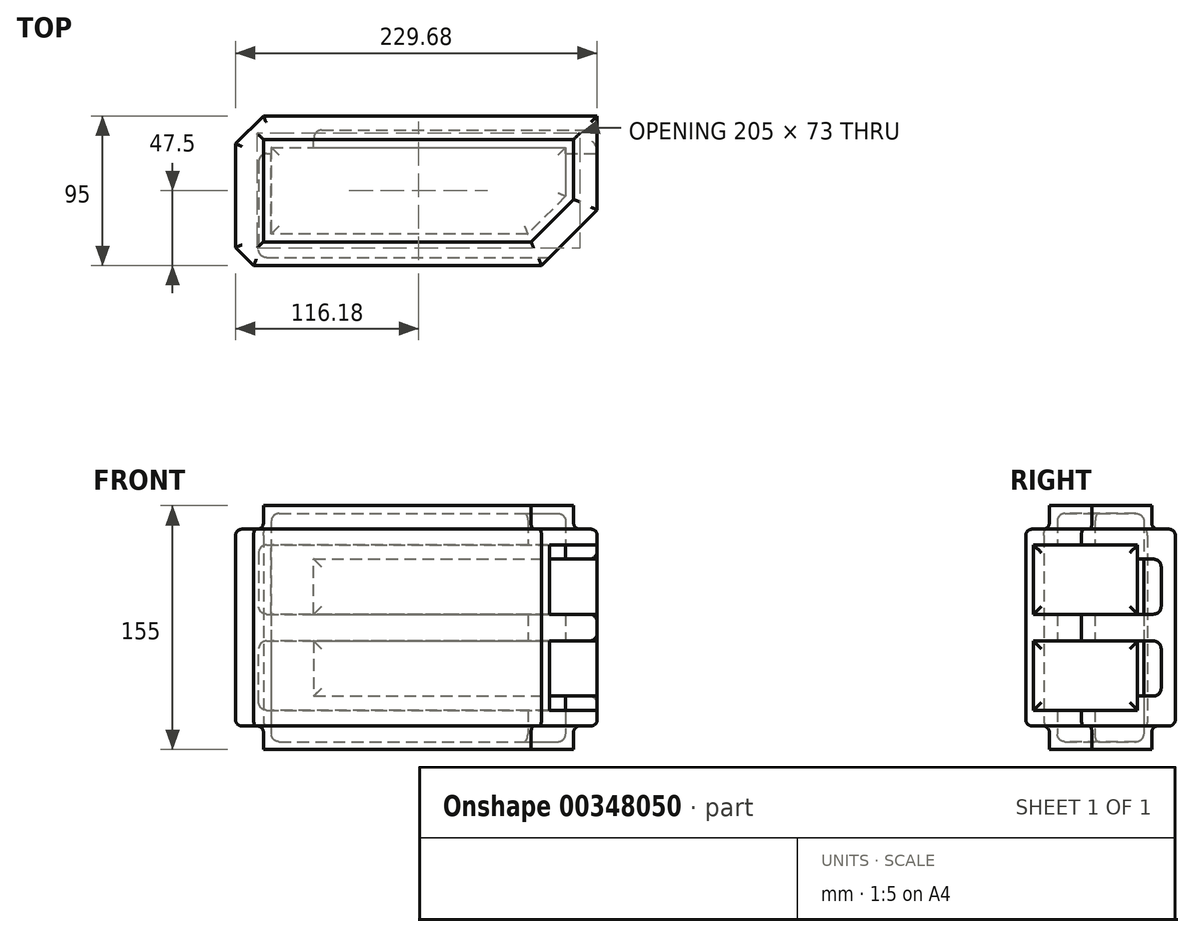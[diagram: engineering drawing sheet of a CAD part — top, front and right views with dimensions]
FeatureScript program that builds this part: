
annotation { "Feature Type Name" : "Feature", "Feature Type Description" : "" }
export const myFeature = defineFeature(function(context is Context, id is Id, definition is map)
    precondition{}
    {
        {
            var Q0;
            Q0=qCreatedBy(makeId("Top.planeOp"),FACE);
            var sketch = newSketch(context, id + "F0", { "sketchPlane" : qUnion([Q0])});
            skLineSegment(sketch, "E0", {"start": v(-103.21, -40) * mm, "end": v(79.64, -40) * mm});
            skPoint(sketch, "E1", {"position": v(0, -50) * mm});
            skLineSegment(sketch, "E2", {"start": v(79.64, -40) * mm, "end": v(115, -4.64) * mm});
            skLineSegment(sketch, "E3", {"start": v(115, -4.64) * mm, "end": v(115, 55) * mm});
            skLineSegment(sketch, "E4.2", {"start": v(100, 2) * mm, "end": v(100, 40) * mm});
            skLineSegment(sketch, "E4.4", {"start": v(73, -25) * mm, "end": v(100, 2) * mm});
            skLineSegment(sketch, "E4.5", {"start": v(-97, -25) * mm, "end": v(73, -25) * mm});
            skLineSegment(sketch, "E5.bottom", {"start": v(-97, 40) * mm, "end": v(100, 40) * mm});
            skLineSegment(sketch, "E5.left", {"start": v(-97, 40) * mm, "end": v(-97, -25) * mm});
            skLineSegment(sketch, "E6", {"start": v(-114.68, -28.54) * mm, "end": v(-114.68, 37.32) * mm});
            skLineSegment(sketch, "E7", {"start": v(-114.68, 37.32) * mm, "end": v(-97, 55) * mm});
            skLineSegment(sketch, "E8", {"start": v(-97, 55) * mm, "end": v(115, 55) * mm});
            skLineSegment(sketch, "E9", {"start": v(-114.68, -28.54) * mm, "end": v(-103.21, -40) * mm});
            skLineSegment(sketch, "E10.0", {"start": v(95, 4.07) * mm, "end": v(95, 35) * mm});
            skLineSegment(sketch, "E10.1", {"start": v(-92, 35) * mm, "end": v(95, 35) * mm});
            skLineSegment(sketch, "E10.2", {"start": v(70.93, -20) * mm, "end": v(95, 4.07) * mm});
            skLineSegment(sketch, "E10.3", {"start": v(-92, -20) * mm, "end": v(70.93, -20) * mm});
            skLineSegment(sketch, "E10.4", {"start": v(-92, 35) * mm, "end": v(-92, -20) * mm});
            skSolve(sketch);
        }
        {
            var Q0;
            Q0=makeQuery(id+"F0.imprint","IMPRINT",FACE,{"disambiguationData":[TD([[makeQuery(id+"F0.imprint","IMPRINT",EDGE,{"derivedFrom":sQuery(id+"F0.wireOp",EDGE,"E4.2")}),1.0]])]});
            var Q1;
            Q1=makeQuery(id+"F0.imprint","IMPRINT",FACE,{"disambiguationData":[TD([[makeQuery(id+"F0.imprint","IMPRINT",EDGE,{"derivedFrom":sQuery(id+"F0.wireOp",EDGE,"E10.0")}),1.0]])]});
            extrude(context, id + "F1", {"entities" : qUnion([Q0, Q1]), "depth" : (125 + 30) * mm, "offsetDistance" : 25 * mm});
        }
        {
            var Q0;
            Q0=makeQuery(id+"F0.imprint","IMPRINT",FACE,{"disambiguationData":[TD([[makeQuery(id+"F0.imprint","IMPRINT",EDGE,{"derivedFrom":sQuery(id+"F0.wireOp",EDGE,"E0")}),1.0]])]});
            extrude(context, id + "F2", {"entities" : qUnion([Q0]), "operationType" : NewBodyOperationType.ADD, "depth" : (155 - 15) * mm, "offsetDistance" : 25 * mm, "hasSecondDirection" : true, "secondDirectionOppositeDirection" : false, "secondDirectionDepth" : 15 * mm});
        }
        {
            var Q0;
            Q0=makeQuery(id+"F2.opExtrude","CAP_FACE",FACE,{"disambiguationData":[OSD([sQuery(id+"F0.wireOp",EDGE,"E0"),sQuery(id+"F0.wireOp",EDGE,"E2"),sQuery(id+"F0.wireOp",EDGE,"E3"),sQuery(id+"F0.wireOp",EDGE,"E4.2"),sQuery(id+"F0.wireOp",EDGE,"E4.4"),sQuery(id+"F0.wireOp",EDGE,"E5.bottom"),sQuery(id+"F0.wireOp",EDGE,"E4.5"),sQuery(id+"F0.wireOp",EDGE,"E5.left"),sQuery(id+"F0.wireOp",EDGE,"E6"),sQuery(id+"F0.wireOp",EDGE,"E7"),sQuery(id+"F0.wireOp",EDGE,"E8"),sQuery(id+"F0.wireOp",EDGE,"E9")])],"isStart":false});
            var Q1;
            Q1=makeQuery(id+"F2.opExtrude","CAP_FACE",FACE,{"disambiguationData":[OSD([sQuery(id+"F0.wireOp",EDGE,"E0"),sQuery(id+"F0.wireOp",EDGE,"E2"),sQuery(id+"F0.wireOp",EDGE,"E3"),sQuery(id+"F0.wireOp",EDGE,"E4.2"),sQuery(id+"F0.wireOp",EDGE,"E4.4"),sQuery(id+"F0.wireOp",EDGE,"E5.bottom"),sQuery(id+"F0.wireOp",EDGE,"E4.5"),sQuery(id+"F0.wireOp",EDGE,"E5.left"),sQuery(id+"F0.wireOp",EDGE,"E6"),sQuery(id+"F0.wireOp",EDGE,"E7"),sQuery(id+"F0.wireOp",EDGE,"E8"),sQuery(id+"F0.wireOp",EDGE,"E9")])],"isStart":true});
            fillet(context, id + "F3", {"entities" : qUnion([Q0, Q1]), "radius" : 4 * mm, "tangentPropagation" : true, "allowEdgeOverflow" : false});
        }
        {
            var Q0;
            Q0=makeQuery(id+"F2.opExtrude","SWEPT_FACE",FACE,{"disambiguationData":[OSD([sQuery(id+"F0.wireOp",EDGE,"E3")])]});
            var sketch = newSketch(context, id + "F4", { "sketchPlane" : qUnion([Q0])});
            skLineSegment(sketch, "E11.bottom", {"start": v(31, 130) * mm, "end": v(-35, 130) * mm});
            skLineSegment(sketch, "E11.top", {"start": v(31, 86) * mm, "end": v(-35, 86) * mm});
            skLineSegment(sketch, "E11.left", {"start": v(31, 130) * mm, "end": v(31, 86) * mm});
            skLineSegment(sketch, "E11.right", {"start": v(-35, 130) * mm, "end": v(-35, 86) * mm});
            skLineSegment(sketch, "E12.bottom", {"start": v(31, 25) * mm, "end": v(-35, 25) * mm});
            skLineSegment(sketch, "E12.top", {"start": v(31, 69) * mm, "end": v(-35, 69) * mm});
            skLineSegment(sketch, "E12.left", {"start": v(31, 25) * mm, "end": v(31, 69) * mm});
            skLineSegment(sketch, "E12.right", {"start": v(-35, 25) * mm, "end": v(-35, 69) * mm});
            skLineSegment(sketch, "E13.bottom", {"start": v(31, 86) * mm, "end": v(46, 86) * mm});
            skLineSegment(sketch, "E13.top", {"start": v(31, 121) * mm, "end": v(46, 121) * mm});
            skLineSegment(sketch, "E13.left", {"start": v(31, 86) * mm, "end": v(31, 121) * mm});
            skLineSegment(sketch, "E13.right", {"start": v(46, 86) * mm, "end": v(46, 121) * mm});
            skLineSegment(sketch, "E14.bottom", {"start": v(31, 69) * mm, "end": v(46, 69) * mm});
            skLineSegment(sketch, "E14.top", {"start": v(31, 34) * mm, "end": v(46, 34) * mm});
            skLineSegment(sketch, "E14.left", {"start": v(31, 69) * mm, "end": v(31, 34) * mm});
            skLineSegment(sketch, "E14.right", {"start": v(46, 69) * mm, "end": v(46, 34) * mm});
            skSolve(sketch);
        }
        {
            var Q0;
            {var subQ0=sQuery(id+"F4.wireOp",EDGE,"E11.left");Q0=makeQuery(id+"F4.imprint","IMPRINT",FACE,{"disambiguationData":[TD([[makeQuery(id+"F4.imprint","IMPRINT",EDGE,{"derivedFrom":subQ0}),-1.0]])]});}
            var Q1;
            {var subQ0=sQuery(id+"F4.wireOp",EDGE,"E11.right");Q1=makeQuery(id+"F4.imprint","IMPRINT",FACE,{"disambiguationData":[TD([[makeQuery(id+"F4.imprint","IMPRINT",EDGE,{"derivedFrom":subQ0}),1.0]])]});}
            var Q2;
            {var subQ0=sQuery(id+"F4.wireOp",EDGE,"E12.right");Q2=makeQuery(id+"F4.imprint","IMPRINT",FACE,{"disambiguationData":[TD([[makeQuery(id+"F4.imprint","IMPRINT",EDGE,{"derivedFrom":subQ0}),-1.0]])]});}
            var Q3;
            {var subQ0=sQuery(id+"F4.wireOp",EDGE,"E12.left");Q3=makeQuery(id+"F4.imprint","IMPRINT",FACE,{"disambiguationData":[TD([[makeQuery(id+"F4.imprint","IMPRINT",EDGE,{"derivedFrom":subQ0}),1.0]])]});}
            extrude(context, id + "F5", {"entities" : qUnion([Q0, Q1, Q2, Q3]), "operationType" : NewBodyOperationType.REMOVE, "oppositeDirection" : true, "depth" : 215 * mm, "offsetDistance" : 25 * mm});
        }
        {
            var Q0;
            Q0=makeQuery(id+"F4.imprint","IMPRINT",FACE,{"disambiguationData":[TD([[makeQuery(id+"F4.imprint","IMPRINT",EDGE,{"derivedFrom":sQuery(id+"F4.wireOp",EDGE,"E14.bottom")}),-1.0]])]});
            var Q1;
            Q1=makeQuery(id+"F4.imprint","IMPRINT",FACE,{"disambiguationData":[TD([[makeQuery(id+"F4.imprint","IMPRINT",EDGE,{"derivedFrom":sQuery(id+"F4.wireOp",EDGE,"E13.bottom")}),1.0]])]});
            extrude(context, id + "F6", {"entities" : qUnion([Q0, Q1]), "operationType" : NewBodyOperationType.REMOVE, "oppositeDirection" : true, "depth" : 180 * mm, "offsetDistance" : 25 * mm});
        }
        {
            var Q0;
            Q0=makeQuery(id+"F0.imprint","IMPRINT",FACE,{"disambiguationData":[TD([[makeQuery(id+"F0.imprint","IMPRINT",EDGE,{"derivedFrom":sQuery(id+"F0.wireOp",EDGE,"E10.0")}),1.0]])]});
            extrude(context, id + "F7", {"entities" : qUnion([Q0]), "operationType" : NewBodyOperationType.REMOVE, "depth" : 150 * mm, "offsetDistance" : 25 * mm, "hasSecondDirection" : true, "secondDirectionOppositeDirection" : false, "secondDirectionDepth" : 5 * mm});
        }
        {
            var Q0;
            Q0=makeQuery(id+"F6.boolean.opBoolean","COPY",EDGE,{"derivedFrom":makeQuery(id+"F6.opExtrude","CAP_EDGE",EDGE,{"disambiguationData":[OSD([sQuery(id+"F4.wireOp",EDGE,"E13.left")])],"isStart":false})});
            var Q1;
            Q1=makeQuery(id+"F6.boolean.opBoolean","COPY",EDGE,{"derivedFrom":makeQuery(id+"F6.opExtrude","SWEPT_EDGE",EDGE,{"disambiguationData":[OSD([sQuery(id+"F4.wireOp",EDGE,"E11.left"),sQuery(id+"F4.wireOp",EDGE,"E13.top"),sQuery(id+"F4.wireOp",EDGE,"E13.left")])]})});
            var Q2;
            Q2=makeQuery(id+"F6.boolean.opBoolean","COPY",EDGE,{"derivedFrom":makeQuery(id+"F6.opExtrude","CAP_EDGE",EDGE,{"disambiguationData":[OSD([sQuery(id+"F4.wireOp",EDGE,"E14.left")])],"isStart":false})});
            var Q3;
            Q3=makeQuery(id+"F6.boolean.opBoolean","COPY",EDGE,{"derivedFrom":makeQuery(id+"F6.opExtrude","SWEPT_EDGE",EDGE,{"disambiguationData":[OSD([sQuery(id+"F4.wireOp",EDGE,"E12.left"),sQuery(id+"F4.wireOp",EDGE,"E14.top"),sQuery(id+"F4.wireOp",EDGE,"E14.left")])]})});
            var Q4;
            Q4=makeQuery(id+"F5.boolean.opBoolean","COPY",FACE,{"derivedFrom":makeQuery(id+"F5.opExtrude","CAP_FACE",FACE,{"disambiguationData":[OSD([sQuery(id+"F4.wireOp",EDGE,"E11.bottom"),sQuery(id+"F4.wireOp",EDGE,"E11.top"),sQuery(id+"F4.wireOp",EDGE,"E11.left"),sQuery(id+"F4.wireOp",EDGE,"E11.right"),sQuery(id+"F4.wireOp",EDGE,"E13.left")])],"isStart":false})});
            var Q5;
            Q5=makeQuery(id+"F5.boolean.opBoolean","COPY",FACE,{"derivedFrom":makeQuery(id+"F5.opExtrude","CAP_FACE",FACE,{"disambiguationData":[OSD([sQuery(id+"F4.wireOp",EDGE,"E12.bottom"),sQuery(id+"F4.wireOp",EDGE,"E12.top"),sQuery(id+"F4.wireOp",EDGE,"E12.left"),sQuery(id+"F4.wireOp",EDGE,"E12.right"),sQuery(id+"F4.wireOp",EDGE,"E14.left")])],"isStart":false})});
            var Q6;
            Q6=makeQuery(id+"F7.boolean.opBoolean","COPY",FACE,{"derivedFrom":makeQuery(id+"F7.opExtrude","CAP_FACE",FACE,{"disambiguationData":[OSD([sQuery(id+"F0.wireOp",EDGE,"E10.0"),sQuery(id+"F0.wireOp",EDGE,"E10.1"),sQuery(id+"F0.wireOp",EDGE,"E10.2"),sQuery(id+"F0.wireOp",EDGE,"E10.3"),sQuery(id+"F0.wireOp",EDGE,"E10.4")])],"isStart":true})});
            var Q7;
            Q7=makeQuery(id+"F7.boolean.opBoolean","COPY",FACE,{"derivedFrom":makeQuery(id+"F7.opExtrude","CAP_FACE",FACE,{"disambiguationData":[OSD([sQuery(id+"F0.wireOp",EDGE,"E10.0"),sQuery(id+"F0.wireOp",EDGE,"E10.1"),sQuery(id+"F0.wireOp",EDGE,"E10.2"),sQuery(id+"F0.wireOp",EDGE,"E10.3"),sQuery(id+"F0.wireOp",EDGE,"E10.4")])],"isStart":false})});
            var Q8;
            Q8=makeQuery(id+"F6.boolean.opBoolean","COPY",FACE,{"derivedFrom":makeQuery(id+"F6.opExtrude","SWEPT_FACE",FACE,{"disambiguationData":[OSD([sQuery(id+"F4.wireOp",EDGE,"E13.right")])]})});
            var Q9;
            Q9=makeQuery(id+"F6.boolean.opBoolean","COPY",FACE,{"derivedFrom":makeQuery(id+"F6.opExtrude","SWEPT_FACE",FACE,{"disambiguationData":[OSD([sQuery(id+"F4.wireOp",EDGE,"E14.right")])]})});
            fillet(context, id + "F8", {"entities" : qUnion([Q0, Q1, Q2, Q3, Q4, Q5, Q6, Q7, Q8, Q9]), "radius" : 5 * mm, "tangentPropagation" : true, "allowEdgeOverflow" : false});
        }
    });
